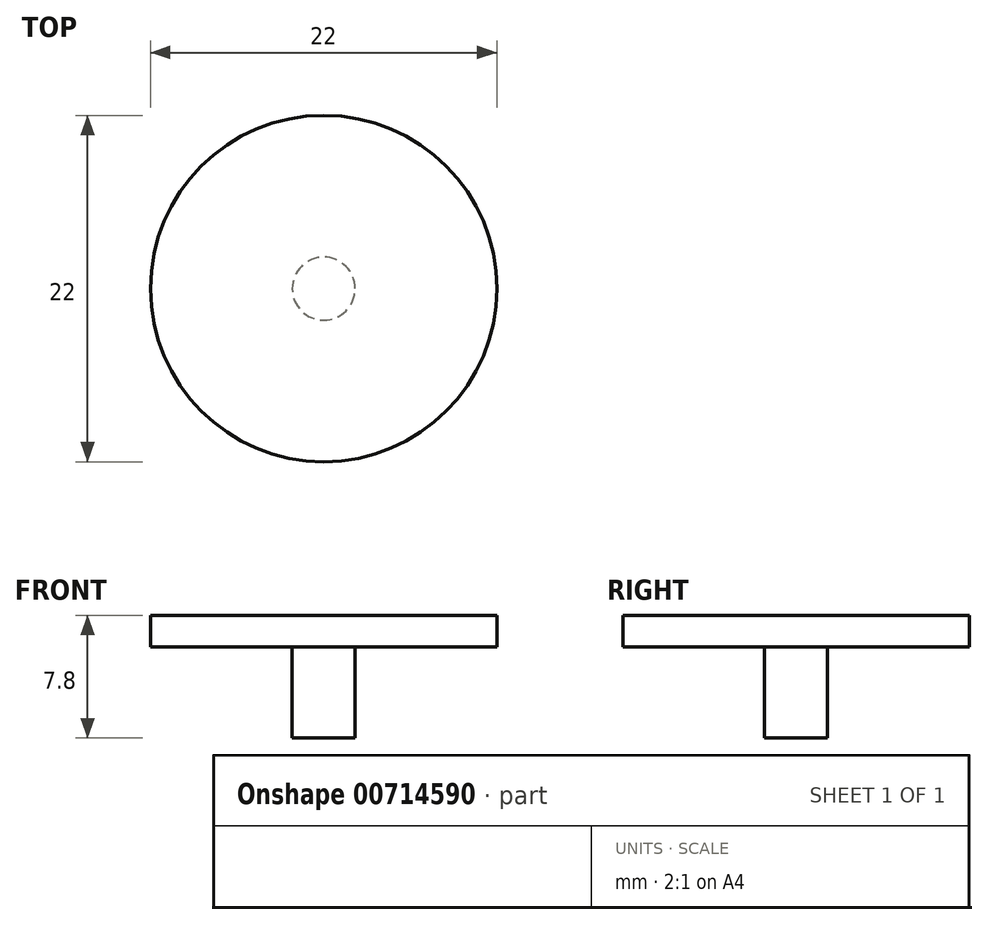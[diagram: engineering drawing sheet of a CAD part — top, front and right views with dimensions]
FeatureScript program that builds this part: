
annotation { "Feature Type Name" : "Feature", "Feature Type Description" : "" }
export const myFeature = defineFeature(function(context is Context, id is Id, definition is map)
    precondition{}
    {
        {
            var Q0;
            Q0=qCreatedBy(makeId("Top.planeOp"),FACE);
            var sketch = newSketch(context, id + "F0", { "sketchPlane" : qUnion([Q0])});
            skCircle(sketch, "E0", {"center": v(0, 0) * mm, "radius": 11 * mm});
            skSolve(sketch);
        }
        {
            var Q0;
            Q0=makeQuery(id+"F0.imprint","IMPRINT",FACE,{"disambiguationData":[TD([[makeQuery(id+"F0.imprint","IMPRINT",EDGE,{"derivedFrom":sQuery(id+"F0.wireOp",EDGE,"E0")}),1.0]])]});
            extrude(context, id + "F1", {"entities" : qUnion([Q0]), "depth" : 2 * mm, "offsetDistance" : 25 * mm});
        }
        {
            var Q0;
            Q0=makeQuery(id+"F1.opExtrude","CAP_FACE",FACE,{"disambiguationData":[OSD([sQuery(id+"F0.wireOp",EDGE,"E0")])],"isStart":true});
            var sketch = newSketch(context, id + "F2", { "sketchPlane" : qUnion([Q0])});
            skCircle(sketch, "E1", {"center": v(0, 0) * mm, "radius": 2 * mm});
            skSolve(sketch);
        }
        {
            var Q0;
            Q0 = qSketchRegion(id + "F2", true);
            extrude(context, id + "F3", {"entities" : qUnion([Q0]), "operationType" : NewBodyOperationType.ADD, "depth" : 5.8 * mm, "offsetDistance" : 25 * mm});
        }
        {
            var Q0;
            Q0=makeQuery(id+"F1.opExtrude","CAP_FACE",FACE,{"disambiguationData":[OSD([sQuery(id+"F0.wireOp",EDGE,"E0")])],"isStart":false});
            var sketch = newSketch(context, id + "F4", { "sketchPlane" : qUnion([Q0])});
            skText(sketch, "E2", { "text": "Lewis\n", "fontName": "OpenSans-Regular.ttf"});
            const initialGuessF4  = {"E2": [-0.00945, -0.00262, 1, 0, 0.00527]};
            skSetInitialGuess(sketch, initialGuessF4);
            skSolve(sketch);
        }
        {
            var Q0;
            Q0 = qSketchRegion(id + "F4", true);
            extrude(context, id + "F5", {"entities" : qUnion([Q0]), "operationType" : NewBodyOperationType.ADD, "oppositeDirection" : true, "depth" : 1 * mm, "offsetDistance" : 25 * mm});
        }
    });
